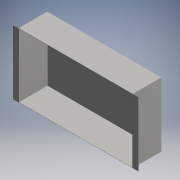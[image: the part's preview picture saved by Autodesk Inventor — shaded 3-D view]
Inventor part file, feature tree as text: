
AUTODESK INVENTOR PART (.ipt)
format: ipt  version: 2018 (Build 220112000, 112)  size: 115,200 bytes
history: native  units: mm (DEFAULTED — no unit token found)
features: extrude x4, sketch x4
ambient origin geometry x8: Origin, YZ Plane, XZ Plane, XY Plane, X Axis, Y Axis, Z Axis, Center Point
bodies: Solid1 (feature_tree)
feature tree (8):
  extrude  "Extrusion1"  Depth=4500.0mm
  extrude  "Extrusion2"  Depth=16.0mm
  extrude  "Extrusion3"  Depth=16.0mm
  extrude  "Extrusion4"  Depth=400.0mm TaperAngle=0.0deg
  sketch  "Sketch1"  dims[d0=7980.0mm d1=4500.0mm]
  sketch  "Sketch2"  dims[d2=1.6mm d3=0.0mm d4=16.0mm]
  sketch  "Sketch3"  dims[d5=2000.0mm d6=0.0mm d7=16.0mm]
  sketch  "Sketch4"  dims[d8=4500.0mm d9=400.0mm d10=0.0mm d11=16.0mm d12=4500.0mm d13=400.0mm d14=0.0mm]
